# Revit family: Washroom-Accessories_Soap-Dispenser-LumeCel-AutoFoam_Rubbermaid
name_source: partatom
category: Generic Models
units: mm (PartAtom-declared; Revit-internal decimal feet)

## family parameters
Can host rebar = No
Cut with Voids When Loaded = No
Host = Face
Maintain Annotation Orientation = No
Part Type = Normal
Room Calculation Point = No
Round Connector Dimension = Use Diameter
Shared = No

## types (6) — shared parameters
CAD Details = https://www.arcat.com
Default Elevation = 4' - 0"
Keynote = 11 82 00
Manufacturer = Rubbermaid Commercial
Product Page URL = https://www.arcat.com
Specification = https://www.arcat.com
URL = https://www.rubbermaidcommercial.com

## per-type parameters (varying)
| type | Body Material | Top Material | Top Material_1 |
| 1980826_AutoFoam Dispenser with LumeCel Technology - Black/Chrome | Rubbermaid_Black | Rubbermaid_Chrome | Rubbermaid_Chrome |
| 1980827_AutoFoam Dispenser with LumeCel Technology - Black/Grey Pearl | Rubbermaid_Black | Rubbermaid_Grey Pearl | Rubbermaid_Grey Pearl |
| 1980828_AutoFoam Dispenser with LumeCel Technology White/Grey Pearl | Rubbermaid_White | Rubbermaid_Grey Pearl | Rubbermaid_Grey Pearl |
| 1980829_AutoFoam Dispenser with LumeCel Technology - Black/Black Pearl | Rubbermaid_Black | Rubbermaid_Black Pearl | Rubbermaid_Black Pearl |
| 1980831_AutoFoam Dispenser with LumeCel Technology - White/Black Pearl | Rubbermaid_White | Rubbermaid_Black Pearl | Rubbermaid_Black Pearl |
| 1980787_AutoFoam Dispenser Retrofit Cover with LumeCel™ Technology - Black/Chrome | Rubbermaid_Black | Rubbermaid_Chrome | Rubbermaid_Chrome |

## geometry (parser evidence)
native form markers: Sweep x2
no freeform markers — native parametric forms only
